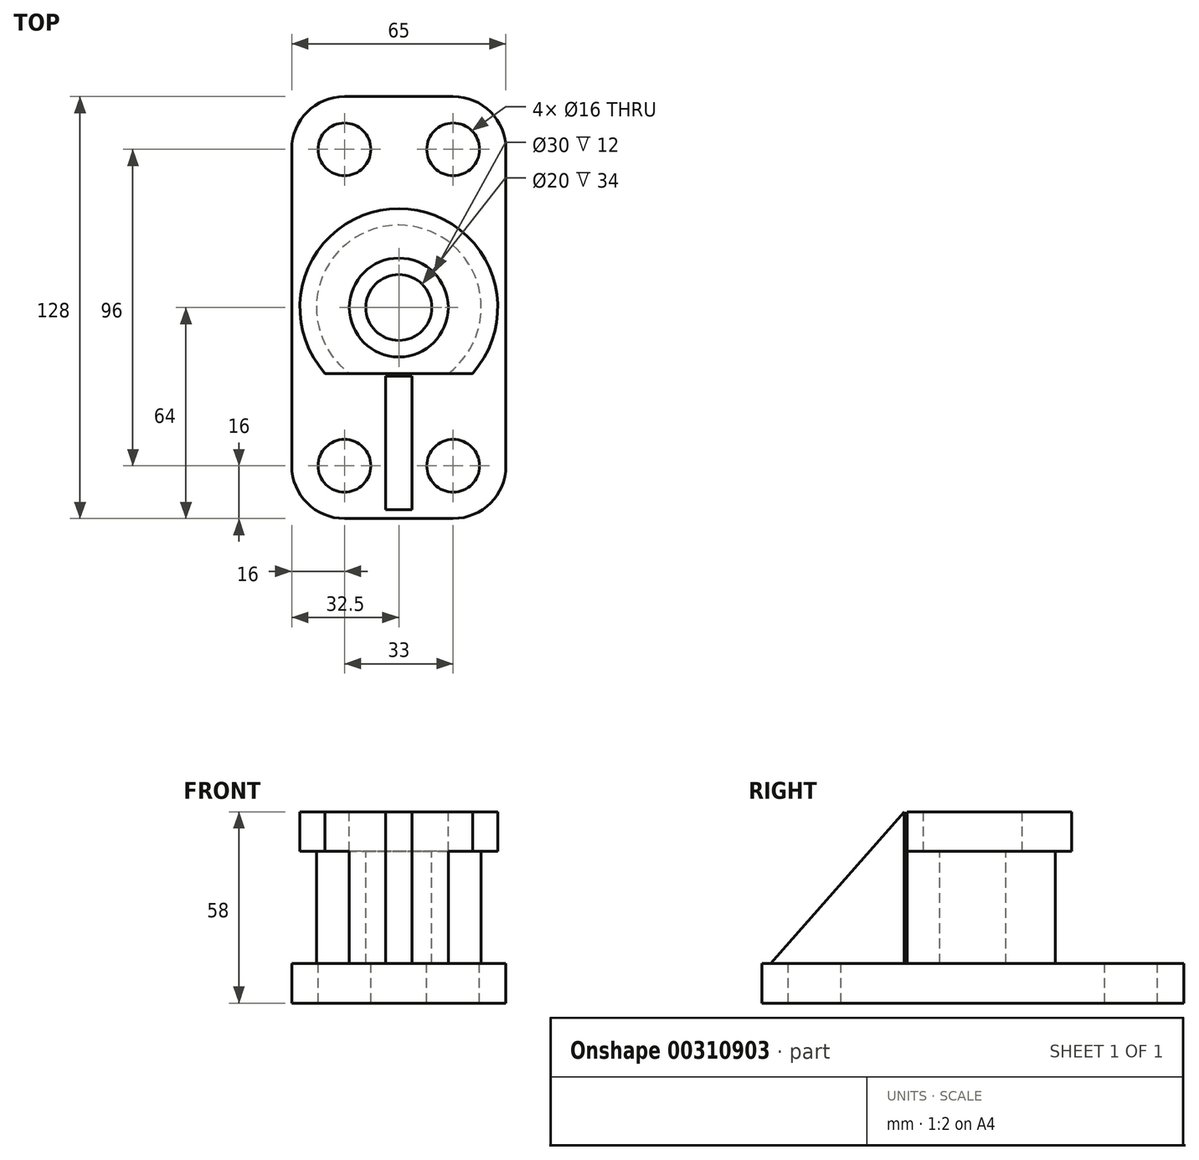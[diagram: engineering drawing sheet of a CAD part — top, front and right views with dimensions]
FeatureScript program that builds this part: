
annotation { "Feature Type Name" : "Feature", "Feature Type Description" : "" }
export const myFeature = defineFeature(function(context is Context, id is Id, definition is map)
    precondition{}
    {
        {
            var Q0;
            Q0=qCreatedBy(makeId("Top.planeOp"),FACE);
            var sketch = newSketch(context, id + "F0", { "sketchPlane" : qUnion([Q0])});
            skCircle(sketch, "E0", {"center": v(0, 0) * mm, "radius": 15 * mm});
            skArc(sketch, "E1", {"start": v(22.36, -20) * mm, "mid": v(0, 30) * mm, "end": v(-22.36, -20) * mm});
            skLineSegment(sketch, "E2", {"start": v(-22.36, -20) * mm, "end": v(22.36, -20) * mm});
            skSolve(sketch);
        }
        {
            var Q0;
            Q0 = qSketchRegion(id + "F0", true);
            extrude(context, id + "F1", {"entities" : qUnion([Q0]), "oppositeDirection" : true, "depth" : 12 * mm});
        }
        {
            var Q0;
            Q0=makeQuery(id+"F1.opExtrude","CAP_FACE",FACE,{"disambiguationData":[OSD([sQuery(id+"F0.wireOp",EDGE,"E0"),sQuery(id+"F0.wireOp",EDGE,"E1"),sQuery(id+"F0.wireOp",EDGE,"E2")])],"isStart":false});
            var sketch = newSketch(context, id + "F2", { "sketchPlane" : qUnion([Q0])});
            skCircle(sketch, "E3", {"center": v(0, 0) * mm, "radius": 10 * mm});
            skArc(sketch, "E4", {"start": v(-15, 20) * mm, "mid": v(0, -25) * mm, "end": v(15, 20) * mm});
            skLineSegment(sketch, "E5", {"start": v(-15, 20) * mm, "end": v(15, 20) * mm});
            skSolve(sketch);
        }
        {
            var Q0;
            Q0 = qSketchRegion(id + "F2", true);
            extrude(context, id + "F3", {"entities" : qUnion([Q0]), "operationType" : NewBodyOperationType.ADD, "depth" : 34 * mm});
        }
        {
            var Q0;
            Q0=makeQuery(id+"F3.opExtrude","CAP_FACE",FACE,{"disambiguationData":[OSD([sQuery(id+"F2.wireOp",EDGE,"E3"),sQuery(id+"F2.wireOp",EDGE,"E4"),sQuery(id+"F2.wireOp",EDGE,"E5")])],"isStart":false});
            var sketch = newSketch(context, id + "F4", { "sketchPlane" : qUnion([Q0])});
            skPoint(sketch, "E6.endSnap0", {"position": v(0, 20) * mm});
            skLineSegment(sketch, "E7", {"start": v(32.5, 64) * mm, "end": v(32.5, 0) * mm});
            skLineSegment(sketch, "E8", {"start": v(0, 64) * mm, "end": v(32.5, 64) * mm});
            skLineSegment(sketch, "E9", {"start": v(32.5, -64) * mm, "end": v(32.5, 0) * mm});
            skLineSegment(sketch, "E10", {"start": v(32.5, -64) * mm, "end": v(0, -64) * mm});
            skLineSegment(sketch, "E11", {"start": v(-32.5, -64) * mm, "end": v(0, -64) * mm});
            skLineSegment(sketch, "E12", {"start": v(-32.5, 0) * mm, "end": v(-32.5, -64) * mm});
            skLineSegment(sketch, "E13", {"start": v(-32.5, 64) * mm, "end": v(-32.5, 0) * mm});
            skLineSegment(sketch, "E14", {"start": v(-32.5, 64) * mm, "end": v(0, 64) * mm});
            skLineSegment(sketch, "E15", {"start": v(0, 0) * mm, "end": v(32.5, 0) * mm});
            skLineSegment(sketch, "E16", {"start": v(0, 0) * mm, "end": v(-32.5, 0) * mm});
            skLineSegment(sketch, "E17", {"start": v(0, 0) * mm, "end": v(0, 64) * mm});
            skLineSegment(sketch, "E18", {"start": v(0, 0) * mm, "end": v(0, -64) * mm});
            skSolve(sketch);
        }
        {
            var Q0;
            Q0 = qSketchRegion(id + "F4", true);
            extrude(context, id + "F5", {"entities" : qUnion([Q0]), "operationType" : NewBodyOperationType.ADD, "depth" : 12 * mm});
        }
        {
            var Q0;
            Q0=makeQuery(id+"F5.opExtrude","SWEPT_EDGE",EDGE,{"disambiguationData":[OSD([sQuery(id+"F4.wireOp",EDGE,"E11"),sQuery(id+"F4.wireOp",EDGE,"E12")])]});
            var Q1;
            Q1=makeQuery(id+"F5.opExtrude","SWEPT_EDGE",EDGE,{"disambiguationData":[OSD([sQuery(id+"F4.wireOp",EDGE,"E9"),sQuery(id+"F4.wireOp",EDGE,"E10")])]});
            var Q2;
            Q2=makeQuery(id+"F5.opExtrude","SWEPT_EDGE",EDGE,{"disambiguationData":[OSD([sQuery(id+"F4.wireOp",EDGE,"E13"),sQuery(id+"F4.wireOp",EDGE,"E14")])]});
            var Q3;
            Q3=makeQuery(id+"F5.opExtrude","SWEPT_EDGE",EDGE,{"disambiguationData":[OSD([sQuery(id+"F4.wireOp",EDGE,"E7"),sQuery(id+"F4.wireOp",EDGE,"E8")])]});
            fillet(context, id + "F6", {"entities" : qUnion([Q0, Q1, Q2, Q3]), "radius" : 16 * mm, "tangentPropagation" : true, "allowEdgeOverflow" : false});
        }
        {
            var Q0;
            {var subQ0=sQuery(id+"F4.wireOp",EDGE,"E9");var subQ1=sQuery(id+"F4.wireOp",EDGE,"E7");var subQ2=sQuery(id+"F4.wireOp",EDGE,"E14");var subQ3=sQuery(id+"F4.wireOp",EDGE,"E8");var subQ4=sQuery(id+"F4.wireOp",EDGE,"E11");var subQ5=sQuery(id+"F4.wireOp",EDGE,"E10");var subQ6=sQuery(id+"F4.wireOp",EDGE,"E13");var subQ7=sQuery(id+"F4.wireOp",EDGE,"E12");Q0=makeQuery(id+"F5.boolean.opBoolean","SPLIT",FACE,{"disambiguationData":[TD([makeQuery(id+"F1.opExtrude","SWEPT_FACE",FACE,{"disambiguationData":[OSD([sQuery(id+"F0.wireOp",EDGE,"E2")])]})])],"derivedFrom":makeQuery(id+"F5.opExtrude","CAP_FACE",FACE,{"disambiguationData":[OSD([subQ1,subQ3,subQ0,subQ5,subQ4,subQ7,subQ6,subQ2])],"isStart":true})});}
            var sketch = newSketch(context, id + "F7", { "sketchPlane" : qUnion([Q0])});
            skPoint(sketch, "E19.endSnap0", {"position": v(0, 64) * mm});
            skPoint(sketch, "E20.endSnap0", {"position": v(0, -64) * mm});
            skCircle(sketch, "E21", {"center": v(16.5, 48) * mm, "radius": 8 * mm});
            skCircle(sketch, "E22", {"center": v(-16.5, 48) * mm, "radius": 8 * mm});
            skCircle(sketch, "E23", {"center": v(-16.5, -48) * mm, "radius": 8 * mm});
            skCircle(sketch, "E24", {"center": v(16.5, -48) * mm, "radius": 8 * mm});
            skSolve(sketch);
        }
        {
            var Q0;
            Q0 = qSketchRegion(id + "F7", true);
            extrude(context, id + "F8", {"entities" : qUnion([Q0]), "operationType" : NewBodyOperationType.REMOVE, "endBound" : BoundingType.THROUGH_ALL, "oppositeDirection" : true, "depth" : 25 * mm});
        }
        {
            var Q0;
            Q0=qCreatedBy(makeId("Right.planeOp"),FACE);
            var sketch = newSketch(context, id + "F9", { "sketchPlane" : qUnion([Q0])});
            skLineSegment(sketch, "E25", {"start": v(-20.8, 0) * mm, "end": v(-20.8, -46.77) * mm});
            skLineSegment(sketch, "E26", {"start": v(-20.8, -46.77) * mm, "end": v(-62.04, -46.77) * mm});
            skLineSegment(sketch, "E27", {"start": v(-62.04, -46.77) * mm, "end": v(-20.8, 0) * mm});
            skSolve(sketch);
        }
        {
            var Q0;
            Q0 = qSketchRegion(id + "F9", true);
            extrude(context, id + "F10", {"entities" : qUnion([Q0]), "operationType" : NewBodyOperationType.ADD, "endBound" : BoundingType.SYMMETRIC, "depth" : 8 * mm});
        }
    });
